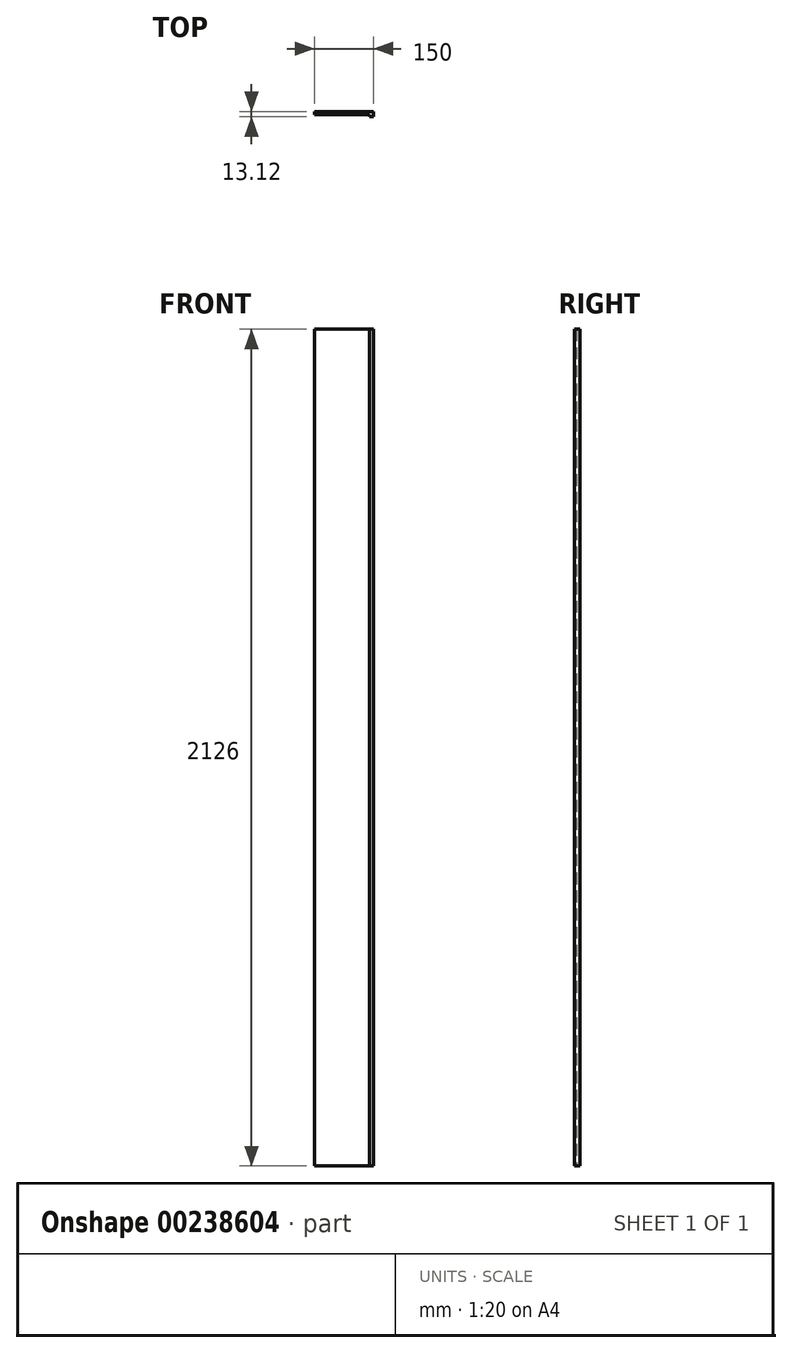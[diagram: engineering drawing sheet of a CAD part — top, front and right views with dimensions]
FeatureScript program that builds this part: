
annotation { "Feature Type Name" : "Feature", "Feature Type Description" : "" }
export const myFeature = defineFeature(function(context is Context, id is Id, definition is map)
    precondition{}
    {
        {
            var Q0;
            Q0=qCreatedBy(makeId("Top.planeOp"),FACE);
            var sketch = newSketch(context, id + "F0", { "sketchPlane" : qUnion([Q0])});
            skLineSegment(sketch, "E0.bottom", {"start": v(0, 0) * mm, "end": v(-150, 0) * mm});
            skLineSegment(sketch, "E0.top", {"start": v(0, 8.12) * mm, "end": v(-150, 8.12) * mm});
            skLineSegment(sketch, "E0.left", {"start": v(0, 0) * mm, "end": v(0, 8.12) * mm});
            skLineSegment(sketch, "E0.right", {"start": v(-150, 0) * mm, "end": v(-150, 8.12) * mm});
            skSolve(sketch);
        }
        {
            var Q0;
            Q0=makeQuery(id+"F0.imprint","IMPRINT",FACE,{"disambiguationData":[TD([[makeQuery(id+"F0.imprint","IMPRINT",EDGE,{"derivedFrom":sQuery(id+"F0.wireOp",EDGE,"E0.bottom")}),-1.0]])]});
            extrude(context, id + "F1", {"entities" : qUnion([Q0]), "depth" : (2000 + 126) * mm});
        }
        {
            var Q0;
            Q0=qCreatedBy(makeId("Top.planeOp"),FACE);
            var sketch = newSketch(context, id + "F2", { "sketchPlane" : qUnion([Q0])});
            skLineSegment(sketch, "E1.bottom", {"start": v(0, 0) * mm, "end": v(-10, 0) * mm});
            skLineSegment(sketch, "E1.top", {"start": v(0, -5) * mm, "end": v(-10, -5) * mm});
            skLineSegment(sketch, "E1.left", {"start": v(0, 0) * mm, "end": v(0, -5) * mm});
            skLineSegment(sketch, "E1.right", {"start": v(-10, 0) * mm, "end": v(-10, -5) * mm});
            skSolve(sketch);
        }
        {
            var Q0;
            Q0 = qSketchRegion(id + "F2", true);
            var Q1;
            Q1=makeQuery(id+"F1.opExtrude","CAP_FACE",FACE,{"disambiguationData":[OSD([sQuery(id+"F0.wireOp",EDGE,"E0.bottom"),sQuery(id+"F0.wireOp",EDGE,"E0.top"),sQuery(id+"F0.wireOp",EDGE,"E0.left"),sQuery(id+"F0.wireOp",EDGE,"E0.right")])],"isStart":false});
            extrude(context, id + "F3", {"entities" : qUnion([Q0]), "operationType" : NewBodyOperationType.ADD, "endBound" : BoundingType.UP_TO_SURFACE, "endBoundEntityFace" : qUnion([Q1]), "depth" : 25 * mm});
        }
    });
